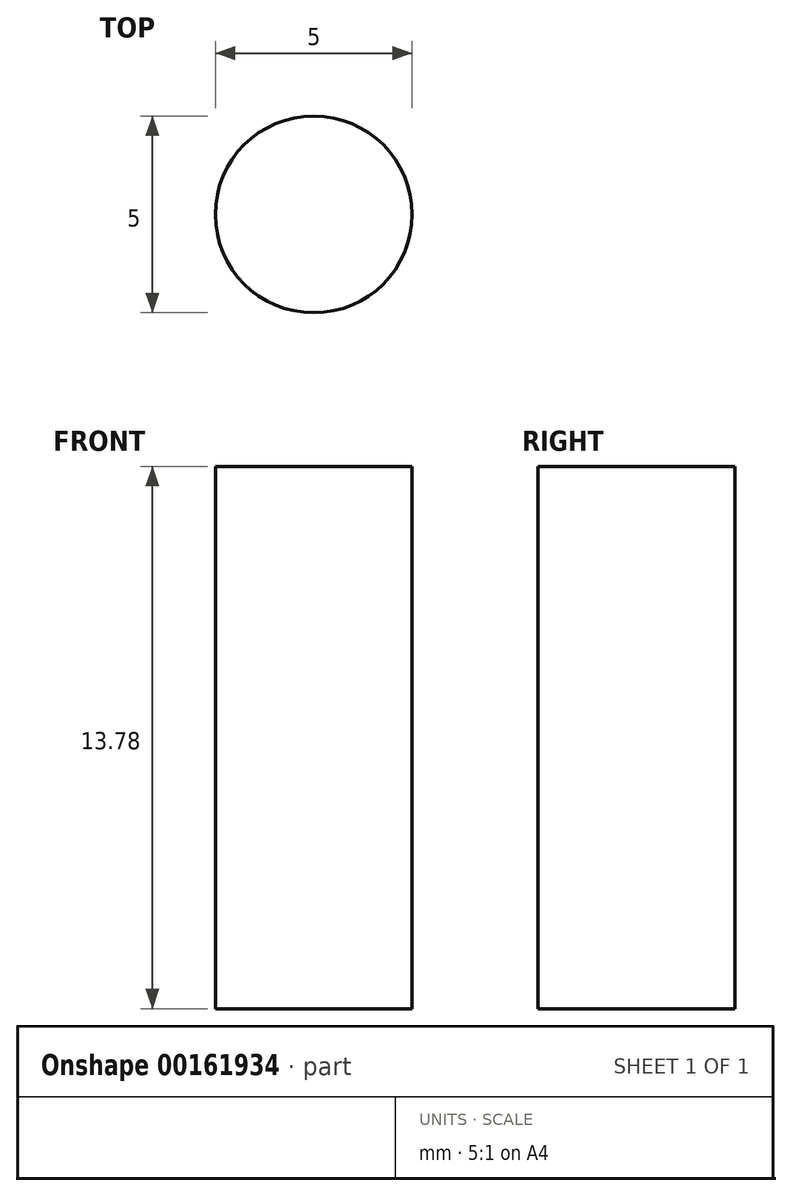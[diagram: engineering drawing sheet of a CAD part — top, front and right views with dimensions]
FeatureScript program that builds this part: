
annotation { "Feature Type Name" : "Feature", "Feature Type Description" : "" }
export const myFeature = defineFeature(function(context is Context, id is Id, definition is map)
    precondition{}
    {
        {
            var Q0;
            Q0=qCreatedBy(makeId("Top.planeOp"),FACE);
            var sketch = newSketch(context, id + "F0", { "sketchPlane" : qUnion([Q0])});
            skCircle(sketch, "E0", {"center": v(0, 0) * mm, "radius": 2.5 * mm});
            skSolve(sketch);
        }
        {
            var Q0;
            Q0 = qSketchRegion(id + "F0", true);
            extrude(context, id + "F1", {"entities" : qUnion([Q0]), "depth" : 13.78 * mm});
        }
    });
